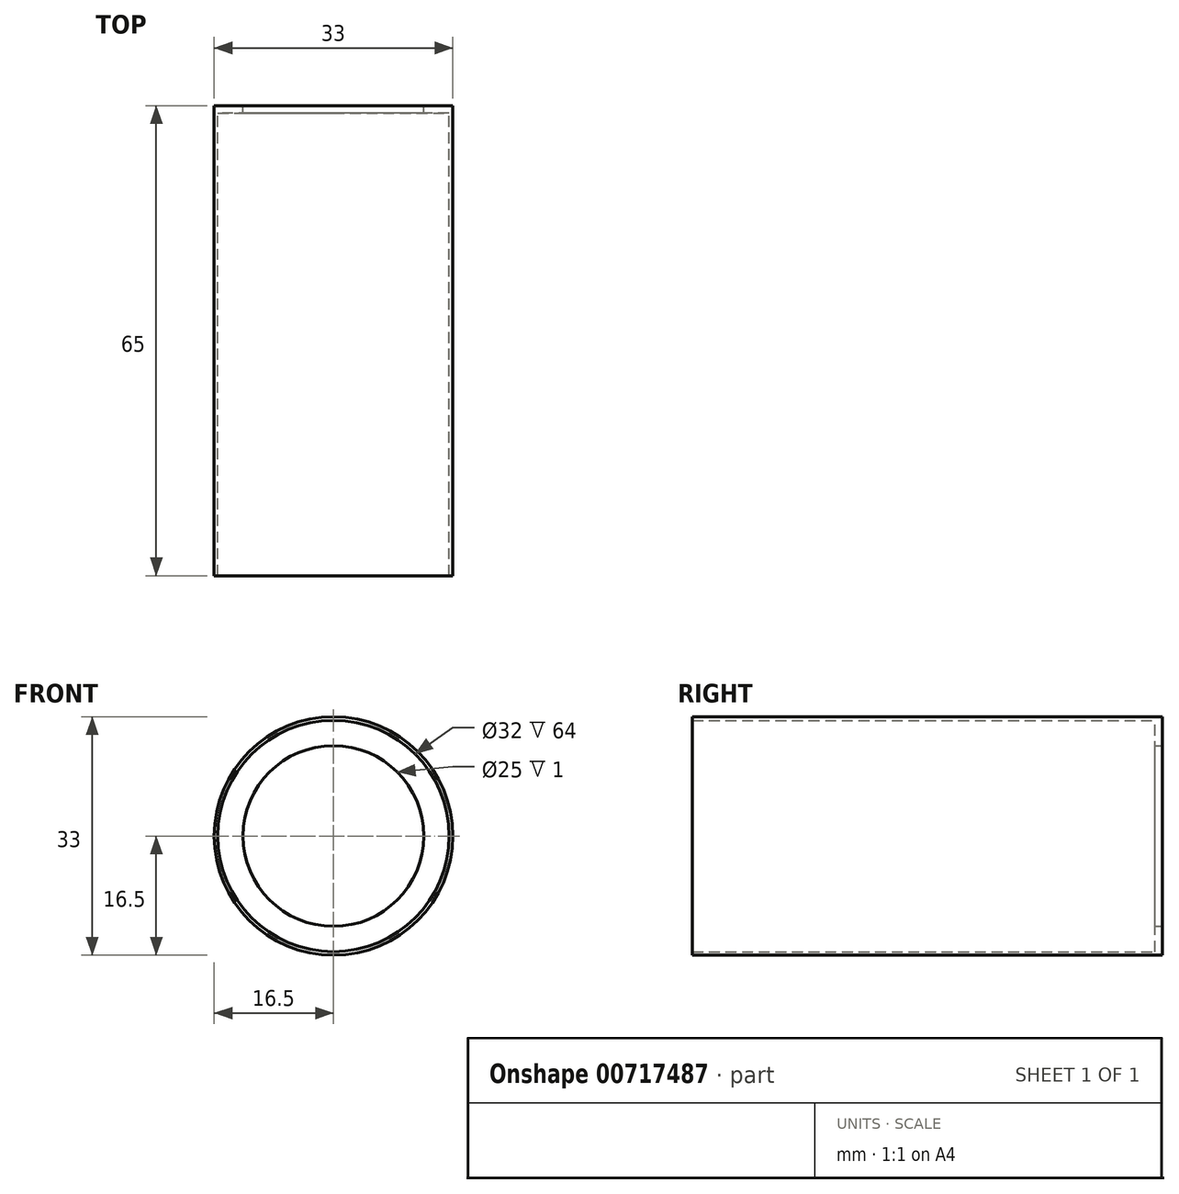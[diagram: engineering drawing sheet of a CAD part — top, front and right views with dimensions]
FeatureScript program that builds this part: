
annotation { "Feature Type Name" : "Feature", "Feature Type Description" : "" }
export const myFeature = defineFeature(function(context is Context, id is Id, definition is map)
    precondition{}
    {
        {
            var Q0;
            Q0=qCreatedBy(makeId("Front.planeOp"),FACE);
            var sketch = newSketch(context, id + "F0", { "sketchPlane" : qUnion([Q0])});
            skCircle(sketch, "E0", {"center": v(0, 0) * mm, "radius": 16 * mm});
            skCircle(sketch, "E1", {"center": v(0, 0) * mm, "radius": 16.5 * mm});
            skSolve(sketch);
        }
        {
            var Q0;
            Q0 = qSketchRegion(id + "F0", true);
            extrude(context, id + "F1", {"entities" : qUnion([Q0]), "depth" : 65 * mm, "offsetDistance" : 25 * mm});
        }
        {
            var Q0;
            Q0=makeQuery(id+"F0.imprint","IMPRINT",FACE,{"disambiguationData":[TD([[makeQuery(id+"F0.imprint","IMPRINT",EDGE,{"derivedFrom":sQuery(id+"F0.wireOp",EDGE,"E0")}),1.0]])]});
            var sketch = newSketch(context, id + "F2", { "sketchPlane" : qUnion([Q0])});
            skCircle(sketch, "E2", {"center": v(0, 0) * mm, "radius": 12.5 * mm});
            skCircle(sketch, "E3", {"center": v(0, 0) * mm, "radius": 16 * mm});
            skSolve(sketch);
        }
        {
            var Q0;
            Q0 = qSketchRegion(id + "F2", true);
            extrude(context, id + "F3", {"entities" : qUnion([Q0]), "operationType" : NewBodyOperationType.ADD, "depth" : 1 * mm, "offsetDistance" : 25 * mm});
        }
    });
